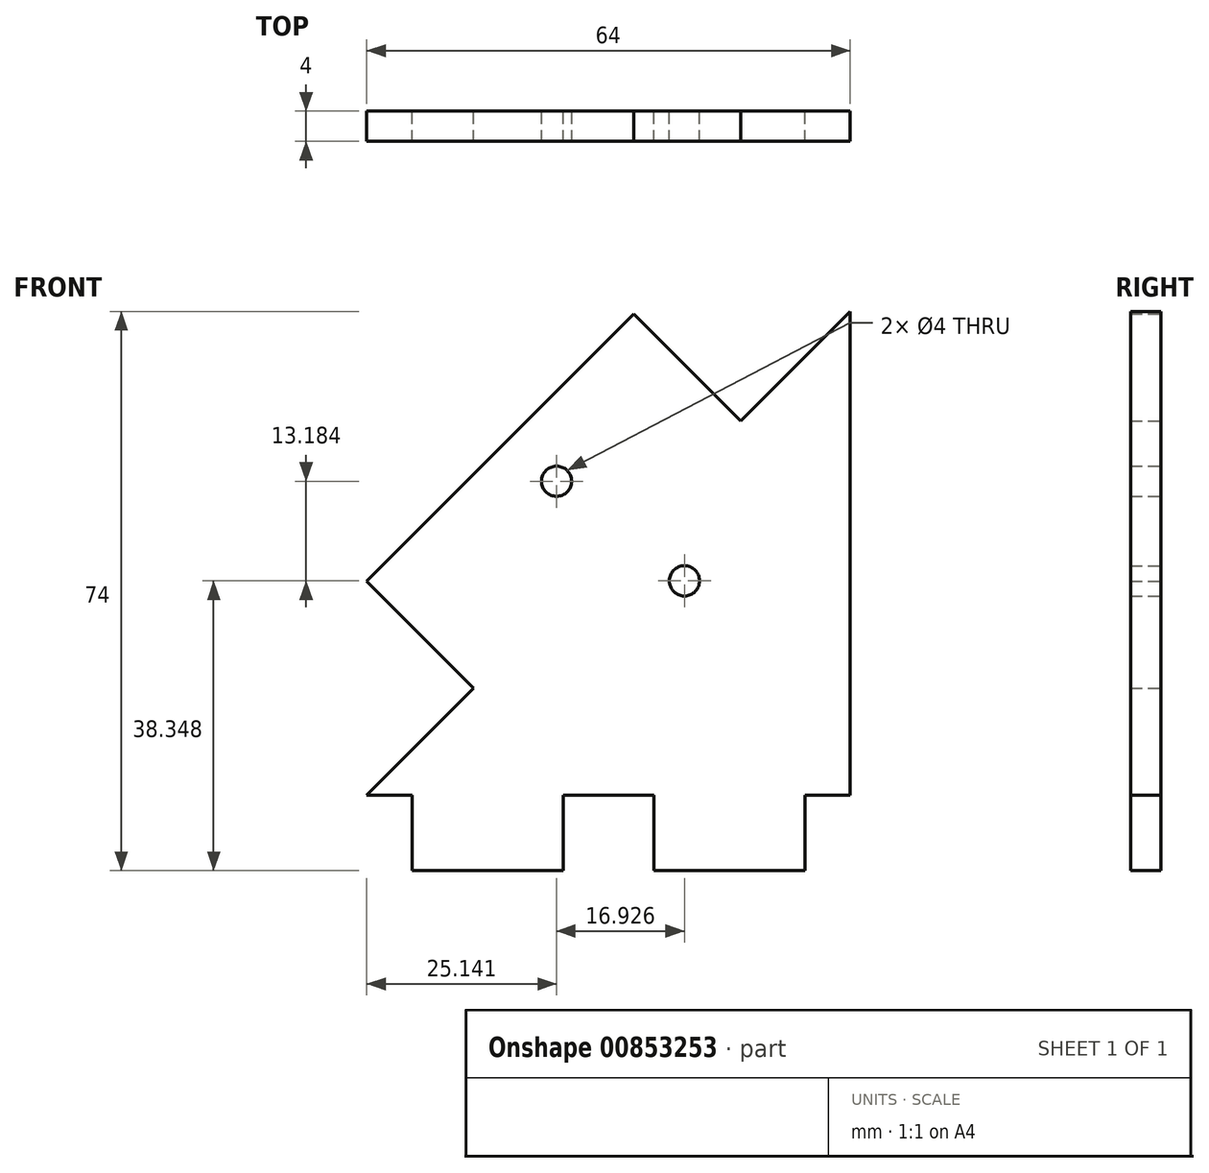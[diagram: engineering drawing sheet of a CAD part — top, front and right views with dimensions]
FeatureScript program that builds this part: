
annotation { "Feature Type Name" : "Feature", "Feature Type Description" : "" }
export const myFeature = defineFeature(function(context is Context, id is Id, definition is map)
    precondition{}
    {
        {
            var Q0;
            Q0=qCreatedBy(makeId("Front.planeOp"),FACE);
            var sketch = newSketch(context, id + "F0", { "sketchPlane" : qUnion([Q0])});
            skLineSegment(sketch, "E0", {"start": v(32, 32) * mm, "end": v(17.5, 17.5) * mm});
            skLineSegment(sketch, "E1", {"start": v(-32, -32) * mm, "end": v(-17.86, -17.86) * mm});
            skLineSegment(sketch, "E2", {"start": v(32, 32) * mm, "end": v(32, -32) * mm});
            skLineSegment(sketch, "E3", {"start": v(-32, -32) * mm, "end": v(-26, -32) * mm});
            skLineSegment(sketch, "E4", {"start": v(-17.86, -17.86) * mm, "end": v(-32, -3.72) * mm});
            skLineSegment(sketch, "E5", {"start": v(-32, -3.72) * mm, "end": v(3.36, 31.64) * mm});
            skLineSegment(sketch, "E6", {"start": v(3.36, 31.64) * mm, "end": v(17.5, 17.5) * mm});
            skLineSegment(sketch, "E7.trimOffspring", {"start": v(-17.86, -17.86) * mm, "end": v(-32, -32) * mm});
            skLineSegment(sketch, "E8.0", {"start": v(-6, -32) * mm, "end": v(-6, -42) * mm});
            skLineSegment(sketch, "E9.0", {"start": v(-26, -42) * mm, "end": v(-6, -42) * mm});
            skLineSegment(sketch, "E10.trimOffspring", {"start": v(-26, -32) * mm, "end": v(-26, -42) * mm});
            skLineSegment(sketch, "E11.trimOffspring", {"start": v(-6, -32) * mm, "end": v(6, -32) * mm});
            skLineSegment(sketch, "E12.MirrorCS", {"start": v(6, -32) * mm, "end": v(6, -42) * mm});
            skLineSegment(sketch, "E13.MirrorCS", {"start": v(26, -42) * mm, "end": v(6, -42) * mm});
            skLineSegment(sketch, "E14.MirrorCS", {"start": v(26, -32) * mm, "end": v(26, -42) * mm});
            skLineSegment(sketch, "E15.trimOffspring", {"start": v(26, -32) * mm, "end": v(32, -32) * mm});
            skCircle(sketch, "E16", {"center": v(10.07, -3.65) * mm, "radius": 2 * mm});
            skCircle(sketch, "E17", {"center": v(-6.86, 9.53) * mm, "radius": 2 * mm});
            skSolve(sketch);
        }
        {
            var Q0;
            Q0 = qSketchRegion(id + "F0", true);
            extrude(context, id + "F1", {"entities" : qUnion([Q0]), "depth" : 4 * mm, "offsetDistance" : 25 * mm});
        }
    });
